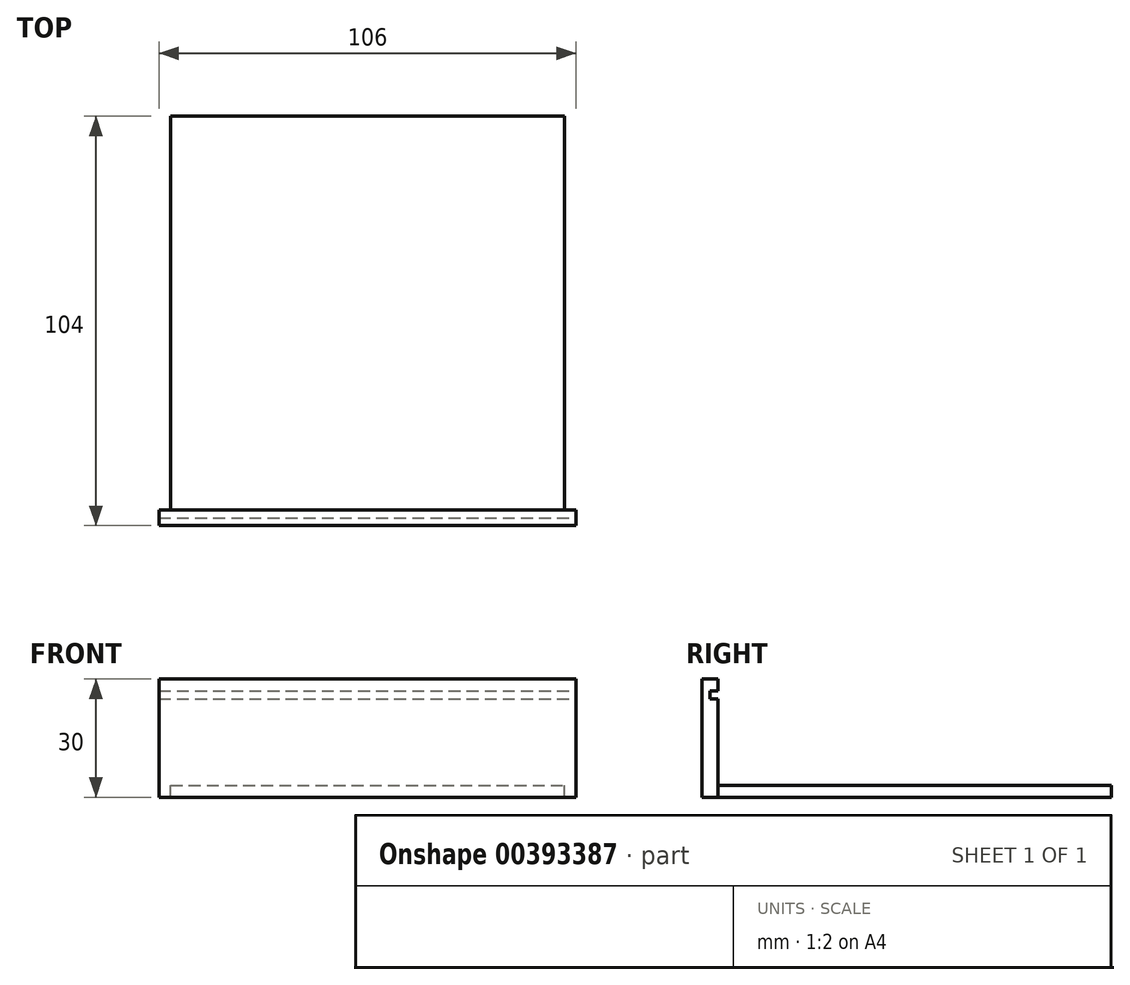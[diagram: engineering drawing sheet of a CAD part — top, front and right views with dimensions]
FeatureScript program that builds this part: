
annotation { "Feature Type Name" : "Feature", "Feature Type Description" : "" }
export const myFeature = defineFeature(function(context is Context, id is Id, definition is map)
    precondition{}
    {
        {
            var Q0;
            Q0=qCreatedBy(makeId("Top.planeOp"),FACE);
            var sketch = newSketch(context, id + "F0", { "sketchPlane" : qUnion([Q0])});
            skLineSegment(sketch, "E0.bottom", {"start": v(-50, 50) * mm, "end": v(50, 50) * mm});
            skLineSegment(sketch, "E0.top", {"start": v(-50, -50) * mm, "end": v(50, -50) * mm});
            skLineSegment(sketch, "E0.left", {"start": v(-50, 50) * mm, "end": v(-50, -50) * mm});
            skLineSegment(sketch, "E0.right", {"start": v(50, 50) * mm, "end": v(50, -50) * mm});
            skPoint(sketch, "E0.middle", {"position": v(0, 0) * mm});
            skSolve(sketch);
        }
        {
            var Q0;
            Q0 = qSketchRegion(id + "F0", true);
            extrude(context, id + "F1", {"entities" : qUnion([Q0]), "oppositeDirection" : true, "depth" : 3 * mm});
        }
        {
            var Q0;
            Q0=makeQuery(id+"F1.opExtrude","SWEPT_FACE",FACE,{"disambiguationData":[OSD([sQuery(id+"F0.wireOp",EDGE,"E0.top")])]});
            var sketch = newSketch(context, id + "F2", { "sketchPlane" : qUnion([Q0])});
            skLineSegment(sketch, "E1.bottom", {"start": v(-53, -3) * mm, "end": v(53, -3) * mm});
            skLineSegment(sketch, "E1.top", {"start": v(-53, 27) * mm, "end": v(53, 27) * mm});
            skLineSegment(sketch, "E1.left", {"start": v(-53, -3) * mm, "end": v(-53, 27) * mm});
            skLineSegment(sketch, "E1.right", {"start": v(53, -3) * mm, "end": v(53, 27) * mm});
            skLineSegment(sketch, "E2", {"start": v(-53, 22) * mm, "end": v(53, 22) * mm});
            skLineSegment(sketch, "E3", {"start": v(-53, 24) * mm, "end": v(53, 24) * mm});
            skSolve(sketch);
        }
        {
            var Q0;
            Q0 = qSketchRegion(id + "F2", true);
            extrude(context, id + "F3", {"entities" : qUnion([Q0]), "operationType" : NewBodyOperationType.ADD, "depth" : 4 * mm});
        }
        {
            var Q0;
            Q0=makeQuery(id+"F3.opExtrude","CAP_FACE",FACE,{"disambiguationData":[OSD([sQuery(id+"F2.wireOp",EDGE,"E1.bottom"),sQuery(id+"F2.wireOp",EDGE,"E1.top"),sQuery(id+"F2.wireOp",EDGE,"E1.left"),sQuery(id+"F2.wireOp",EDGE,"E1.right")])],"isStart":true});
            var sketch = newSketch(context, id + "F4", { "sketchPlane" : qUnion([Q0])});
            skLineSegment(sketch, "E4", {"start": v(53, 22) * mm, "end": v(-53, 22) * mm});
            skLineSegment(sketch, "E5", {"start": v(53, 24) * mm, "end": v(-53, 24) * mm});
            skLineSegment(sketch, "E6", {"start": v(-53, 24) * mm, "end": v(-53, 22) * mm});
            skLineSegment(sketch, "E7", {"start": v(53, 24) * mm, "end": v(53, 22) * mm});
            skSolve(sketch);
        }
        {
            var Q0;
            Q0 = qSketchRegion(id + "F4", true);
            extrude(context, id + "F5", {"entities" : qUnion([Q0]), "operationType" : NewBodyOperationType.REMOVE, "oppositeDirection" : true, "depth" : 2 * mm});
        }
    });
